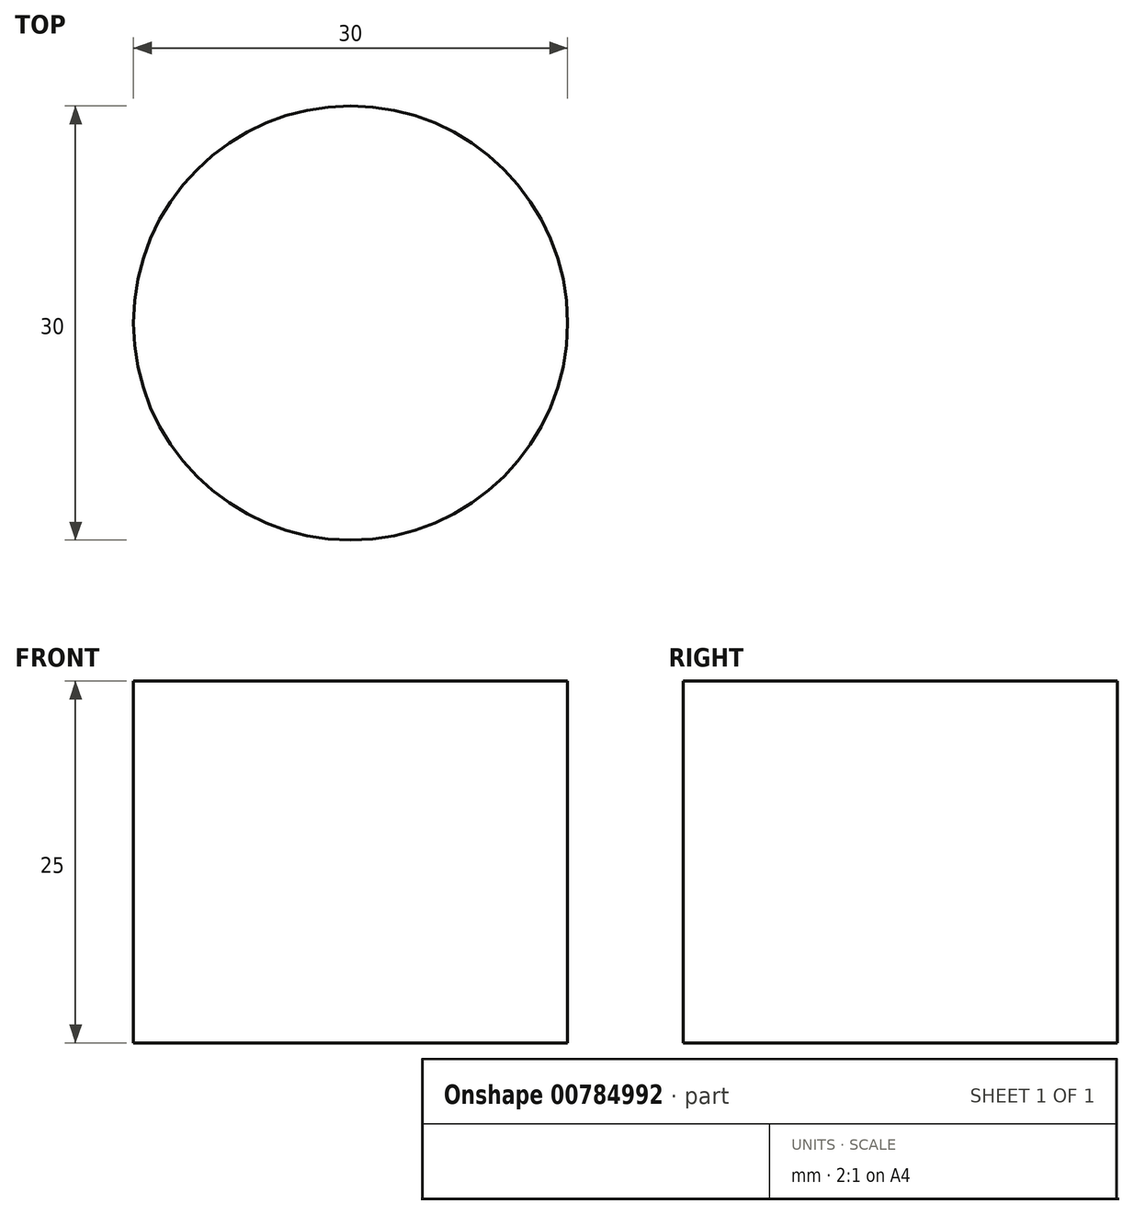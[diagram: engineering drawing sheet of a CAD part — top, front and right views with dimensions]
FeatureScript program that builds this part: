
annotation { "Feature Type Name" : "Feature", "Feature Type Description" : "" }
export const myFeature = defineFeature(function(context is Context, id is Id, definition is map)
    precondition{}
    {
        {
            var Q0;
            Q0=qCreatedBy(makeId("Top.planeOp"),FACE);
            var sketch = newSketch(context, id + "F0", { "sketchPlane" : qUnion([Q0])});
            skCircle(sketch, "E0", {"center": v(0, 0) * mm, "radius": 15 * mm});
            skSolve(sketch);
        }
        {
            var Q0;
            Q0 = qSketchRegion(id + "F0", true);
            var Q1;
            Q1=makeQuery(id+"F0.imprint","IMPRINT",FACE,{"disambiguationData":[TD([[makeQuery(id+"F0.imprint","IMPRINT",EDGE,{"derivedFrom":sQuery(id+"F0.wireOp",EDGE,"E0")}),1.0]])]});
            extrude(context, id + "F1", {"entities" : qUnion([Q0, Q1]), "depth" : 25 * mm, "offsetDistance" : 25 * mm});
        }
    });
